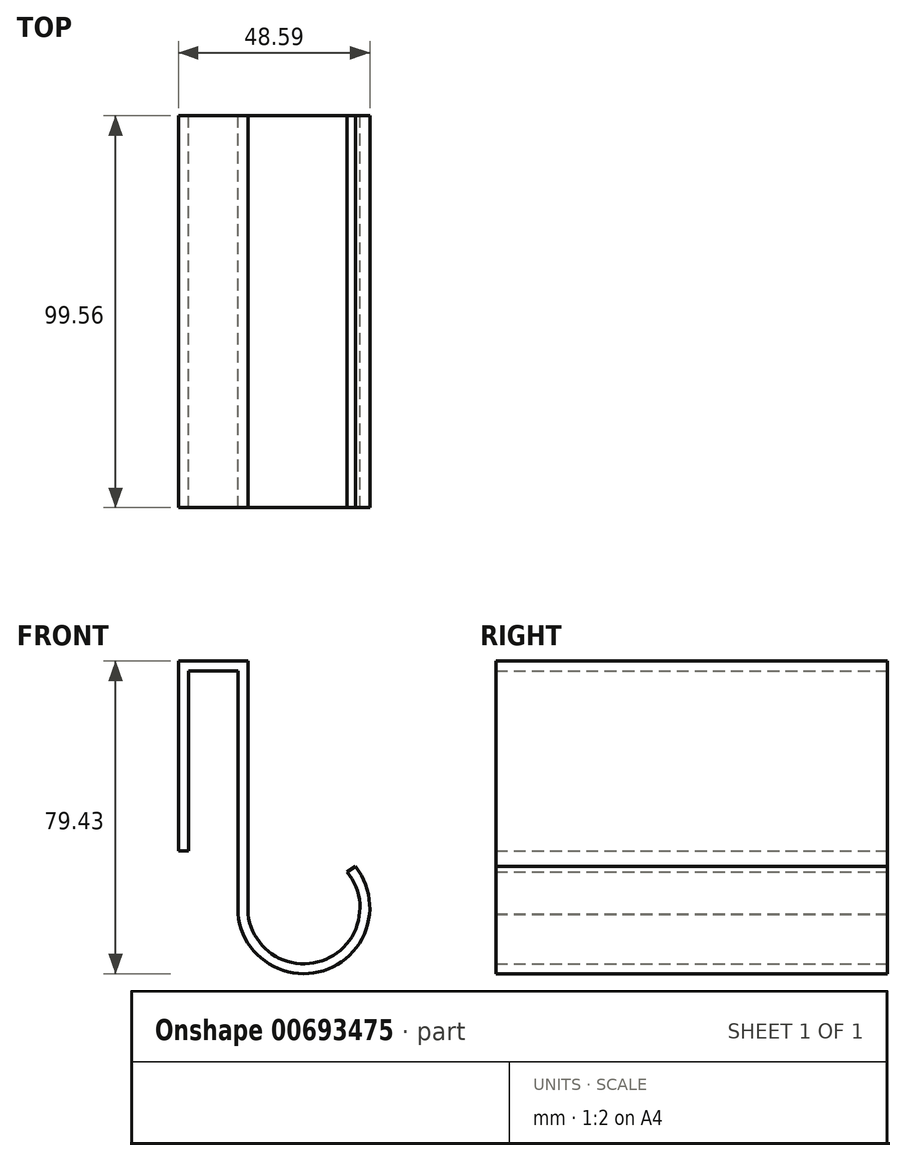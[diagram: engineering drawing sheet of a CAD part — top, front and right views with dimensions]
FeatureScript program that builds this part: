
annotation { "Feature Type Name" : "Feature", "Feature Type Description" : "" }
export const myFeature = defineFeature(function(context is Context, id is Id, definition is map)
    precondition{}
    {
        {
            var Q0;
            Q0=qCreatedBy(makeId("Front.planeOp"),FACE);
            var sketch = newSketch(context, id + "F0", { "sketchPlane" : qUnion([Q0])});
            skLineSegment(sketch, "E0", {"start": v(-40.9, -65.65) * mm, "end": v(-40.9, -127.3) * mm});
            skArc(sketch, "E1", {"start": v(-40.9, -127.3) * mm, "mid": v(-17.96, -141.35) * mm, "end": v(-11.07, -115.33) * mm});
            skLineSegment(sketch, "E2", {"start": v(-40.9, -65.65) * mm, "end": v(-53.48, -65.65) * mm});
            skLineSegment(sketch, "E3", {"start": v(-53.48, -65.65) * mm, "end": v(-53.48, -111.34) * mm});
            skLineSegment(sketch, "E4", {"start": v(-53.48, -111.34) * mm, "end": v(-56, -111.34) * mm});
            skLineSegment(sketch, "E5", {"start": v(-56, -111.34) * mm, "end": v(-56, -63.12) * mm});
            skLineSegment(sketch, "E6", {"start": v(-56, -63.12) * mm, "end": v(-38.38, -63.12) * mm});
            skLineSegment(sketch, "E7", {"start": v(-38.38, -63.12) * mm, "end": v(-38.38, -127.41) * mm});
            skArc(sketch, "E8", {"start": v(-38.38, -127.41) * mm, "mid": v(-18.58, -138.9) * mm, "end": v(-13.24, -116.64) * mm});
            skLineSegment(sketch, "E9.trimOffspring", {"start": v(-13.24, -116.64) * mm, "end": v(-11.07, -115.33) * mm});
            skSolve(sketch);
        }
        {
            var Q0;
            Q0=makeQuery(id+"F0.imprint","IMPRINT",FACE,{"disambiguationData":[TD([[makeQuery(id+"F0.imprint","IMPRINT",EDGE,{"derivedFrom":sQuery(id+"F0.wireOp",EDGE,"E0")}),1.0]])]});
            extrude(context, id + "F1", {"entities" : qUnion([Q0]), "depth" : 99.56 * mm, "offsetDistance" : 25 * mm});
        }
        {
            var Q0;
            Q0=makeQuery(id+"F1.opExtrude","SWEPT_FACE",FACE,{"disambiguationData":[OSD([sQuery(id+"F0.wireOp",EDGE,"E7")])]});
            var sketch = newSketch(context, id + "F2", { "sketchPlane" : qUnion([Q0])});
            skLineSegment(sketch, "E10", {"start": v(-62.61, -144.68) * mm, "end": v(-62.61, -115.4) * mm});
            skLineSegment(sketch, "E11", {"start": v(-37.21, -115.4) * mm, "end": v(-37.21, -144.71) * mm});
            skPoint(sketch, "E12.start.orphan", {"position": v(-49.78, -127.41) * mm});
            skLineSegment(sketch, "E13", {"start": v(-62.61, -144.68) * mm, "end": v(-37.21, -144.71) * mm});
            skLineSegment(sketch, "E14", {"start": v(-62.61, -115.4) * mm, "end": v(-37.21, -115.4) * mm});
            skSolve(sketch);
        }
        {
            var Q0;
            Q0=sQuery(id+"F2.wireOp",EDGE,"E10");
            extrude(context, id + "F3", {"bodyType" : ToolBodyType.SURFACE, "surfaceEntities" : qUnion([Q0]), "depth" : 33.1 * mm, "offsetDistance" : 25 * mm});
        }
        {
            var Q0;
            Q0=sQuery(id+"F2.wireOp",EDGE,"E11");
            extrude(context, id + "F4", {"bodyType" : ToolBodyType.SURFACE, "surfaceEntities" : qUnion([Q0]), "depth" : 33.3 * mm, "offsetDistance" : 25 * mm});
        }
        {
            var Q0;
            Q0=sQuery(id+"F2.wireOp",EDGE,"E13");
            extrude(context, id + "F5", {"bodyType" : ToolBodyType.SURFACE, "surfaceEntities" : qUnion([Q0]), "depth" : 33.4 * mm, "offsetDistance" : 25 * mm});
        }
        {
            var Q0;
            Q0=sQuery(id+"F2.wireOp",EDGE,"E14");
            extrude(context, id + "F6", {"bodyType" : ToolBodyType.SURFACE, "surfaceEntities" : qUnion([Q0]), "depth" : 33.4 * mm, "offsetDistance" : 25 * mm});
        }
    });
